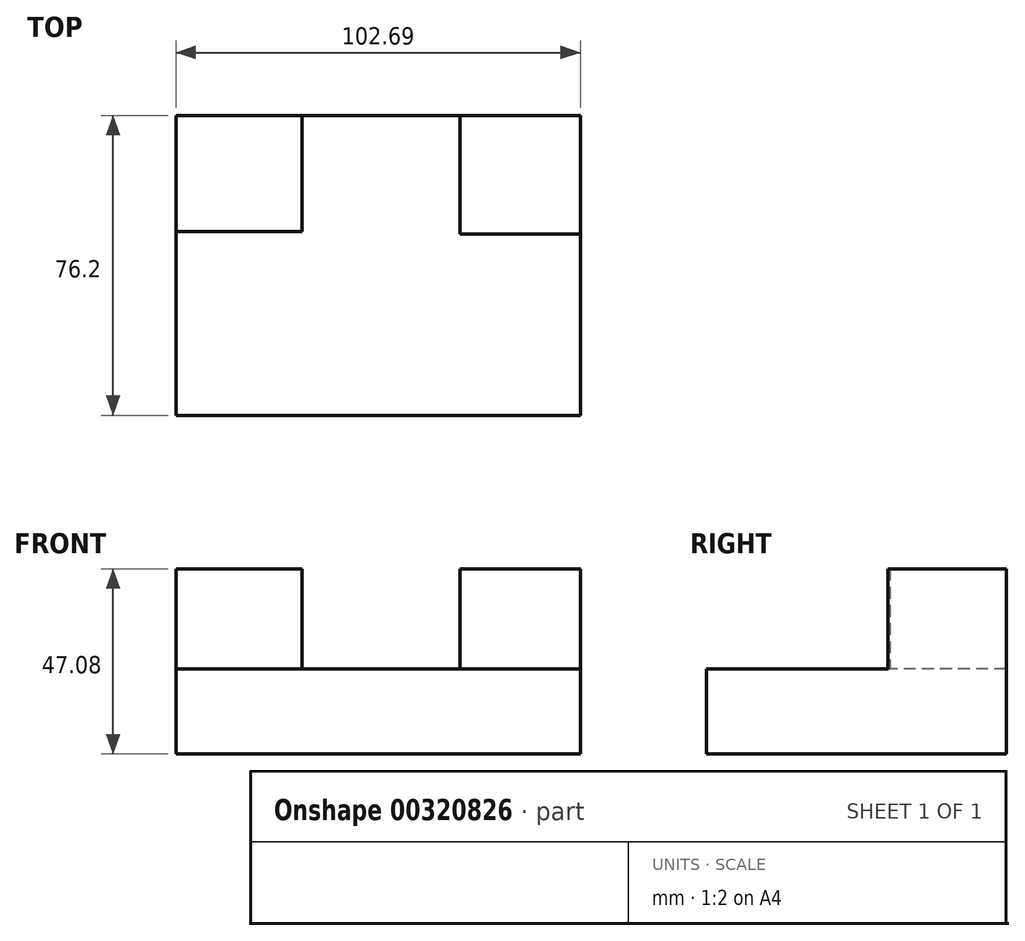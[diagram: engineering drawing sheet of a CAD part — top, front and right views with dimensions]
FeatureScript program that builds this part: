
annotation { "Feature Type Name" : "Feature", "Feature Type Description" : "" }
export const myFeature = defineFeature(function(context is Context, id is Id, definition is map)
    precondition{}
    {
        {
            var Q0;
            Q0=qCreatedBy(makeId("Front.planeOp"),FACE);
            var sketch = newSketch(context, id + "F0", { "sketchPlane" : qUnion([Q0])});
            skLineSegment(sketch, "E0", {"start": v(55.05, -30.1) * mm, "end": v(55.05, -51.77) * mm});
            skLineSegment(sketch, "E1", {"start": v(55.05, -51.77) * mm, "end": v(-47.64, -51.77) * mm});
            skLineSegment(sketch, "E2", {"start": v(-47.64, -51.77) * mm, "end": v(-47.64, -30.1) * mm});
            skLineSegment(sketch, "E3", {"start": v(-47.64, -30.1) * mm, "end": v(55.05, -30.1) * mm});
            skSolve(sketch);
        }
        {
            var Q0;
            Q0=makeQuery(id+"F0.imprint","IMPRINT",FACE,{"disambiguationData":[TD([[makeQuery(id+"F0.imprint","IMPRINT",EDGE,{"derivedFrom":sQuery(id+"F0.wireOp",EDGE,"E0")}),-1.0]])]});
            extrude(context, id + "F1", {"entities" : qUnion([Q0]), "depth" : 76.2 * mm});
        }
        {
            var Q0;
            Q0=makeQuery(id+"F1.opExtrude","SWEPT_FACE",FACE,{"disambiguationData":[OSD([sQuery(id+"F0.wireOp",EDGE,"E3")])]});
            var sketch = newSketch(context, id + "F2", { "sketchPlane" : qUnion([Q0])});
            skLineSegment(sketch, "E4.bottom", {"start": v(24.52, 0) * mm, "end": v(55.05, 0) * mm});
            skLineSegment(sketch, "E4.top", {"start": v(24.52, -30.08) * mm, "end": v(55.05, -30.08) * mm});
            skLineSegment(sketch, "E4.left", {"start": v(24.52, 0) * mm, "end": v(24.52, -30.08) * mm});
            skLineSegment(sketch, "E4.right", {"start": v(55.05, 0) * mm, "end": v(55.05, -30.08) * mm});
            skSolve(sketch);
        }
        {
            var Q0;
            Q0=makeQuery(id+"F2.imprint","IMPRINT",FACE,{"disambiguationData":[TD([[makeQuery(id+"F2.imprint","IMPRINT",EDGE,{"derivedFrom":sQuery(id+"F2.wireOp",EDGE,"E4.bottom")}),-1.0]])]});
            extrude(context, id + "F3", {"entities" : qUnion([Q0]), "operationType" : NewBodyOperationType.ADD, "depth" : 25.4 * mm});
        }
        {
            var Q0;
            Q0=makeQuery(id+"F1.opExtrude","SWEPT_FACE",FACE,{"disambiguationData":[OSD([sQuery(id+"F0.wireOp",EDGE,"E3")])]});
            var sketch = newSketch(context, id + "F4", { "sketchPlane" : qUnion([Q0])});
            skLineSegment(sketch, "E5.bottom", {"start": v(-47.64, 0) * mm, "end": v(-15.69, 0) * mm});
            skLineSegment(sketch, "E5.top", {"start": v(-47.64, -29.52) * mm, "end": v(-15.69, -29.52) * mm});
            skLineSegment(sketch, "E5.left", {"start": v(-47.64, 0) * mm, "end": v(-47.64, -29.52) * mm});
            skLineSegment(sketch, "E5.right", {"start": v(-15.69, 0) * mm, "end": v(-15.69, -29.52) * mm});
            skSolve(sketch);
        }
        {
            var Q0;
            Q0=makeQuery(id+"F4.imprint","IMPRINT",FACE,{"disambiguationData":[TD([[makeQuery(id+"F4.imprint","IMPRINT",EDGE,{"derivedFrom":sQuery(id+"F4.wireOp",EDGE,"E5.bottom")}),-1.0]])]});
            extrude(context, id + "F5", {"entities" : qUnion([Q0]), "operationType" : NewBodyOperationType.ADD, "depth" : 25.4 * mm});
        }
    });
